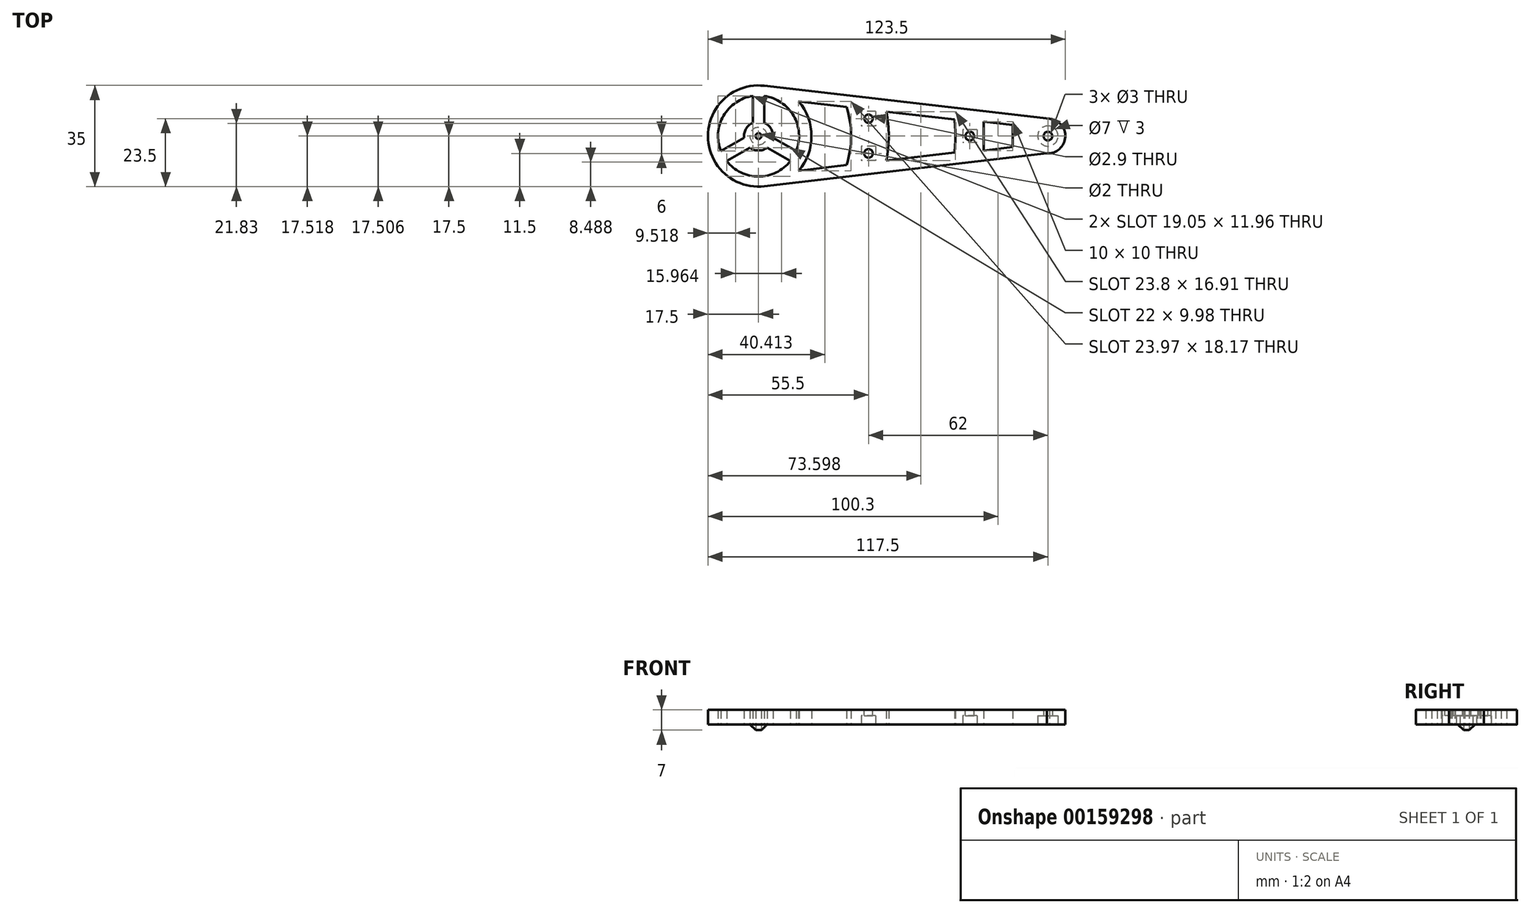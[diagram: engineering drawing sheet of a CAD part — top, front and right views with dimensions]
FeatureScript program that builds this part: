
annotation { "Feature Type Name" : "Feature", "Feature Type Description" : "" }
export const myFeature = defineFeature(function(context is Context, id is Id, definition is map)
    precondition{}
    {
        {
            var Q0;
            Q0=qCreatedBy(makeId("Top.planeOp"),FACE);
            var sketch = newSketch(context, id + "F0", { "sketchPlane" : qUnion([Q0])});
            skArc(sketch, "E0", {"start": v(2.01, 17.38) * mm, "mid": v(-17.5, 0) * mm, "end": v(2.03, -17.38) * mm});
            skArc(sketch, "E1", {"start": v(99.68, -6) * mm, "mid": v(105.99, -0.4) * mm, "end": v(100.47, 5.98) * mm});
            skLineSegment(sketch, "E2", {"start": v(100.47, 5.98) * mm, "end": v(2.01, 17.38) * mm});
            skLineSegment(sketch, "E3", {"start": v(99.68, -6) * mm, "end": v(2.03, -17.38) * mm});
            skArc(sketch, "E4", {"start": v(-2.97, -4.02) * mm, "mid": v(0, -5) * mm, "end": v(2.97, -4.02) * mm});
            skArc(sketch, "E5", {"start": v(-2, 13.86) * mm, "mid": v(-12.12, 7) * mm, "end": v(-13, -5.2) * mm});
            skArc(sketch, "E6", {"start": v(13.84, -11.98) * mm, "mid": v(18.3, 0) * mm, "end": v(13.83, 11.99) * mm});
            skArc(sketch, "E7", {"start": v(30.38, -10.05) * mm, "mid": v(32, 0.01) * mm, "end": v(30.37, 10.07) * mm});
            skLineSegment(sketch, "E8", {"start": v(13.83, 11.99) * mm, "end": v(30.37, 10.07) * mm});
            skLineSegment(sketch, "E9", {"start": v(13.84, -11.98) * mm, "end": v(30.38, -10.05) * mm});
            skLineSegment(sketch, "E10", {"start": v(-2, 13.86) * mm, "end": v(-2, 4.58) * mm});
            skLineSegment(sketch, "E11", {"start": v(2, 13.86) * mm, "end": v(2, 4.58) * mm});
            skLineSegment(sketch, "E12.1.0", {"start": v(-13, -5.2) * mm, "end": v(-4.97, -0.56) * mm});
            skLineSegment(sketch, "E12.1.1", {"start": v(-11, -8.66) * mm, "end": v(-2.97, -4.02) * mm});
            skLineSegment(sketch, "E12.2.0", {"start": v(11, -8.66) * mm, "end": v(2.97, -4.02) * mm});
            skLineSegment(sketch, "E12.2.1", {"start": v(13, -5.2) * mm, "end": v(4.97, -0.56) * mm});
            skArc(sketch, "E13.trimOffspring", {"start": v(13, -5.2) * mm, "mid": v(12.12, 7) * mm, "end": v(2, 13.86) * mm});
            skArc(sketch, "E14.trimOffspring", {"start": v(-11, -8.66) * mm, "mid": v(0, -14) * mm, "end": v(11, -8.66) * mm});
            skArc(sketch, "E15.trimOffspring", {"start": v(4.97, -0.56) * mm, "mid": v(4.33, 2.5) * mm, "end": v(2, 4.58) * mm});
            skArc(sketch, "E16.trimOffspring", {"start": v(-2, 4.58) * mm, "mid": v(-4.33, 2.5) * mm, "end": v(-4.97, -0.56) * mm});
            skCircle(sketch, "E17", {"center": v(0, 0) * mm, "radius": 1.5 * mm});
            skLineSegment(sketch, "E18", {"start": v(77.8, 5) * mm, "end": v(77.8, -5) * mm});
            skLineSegment(sketch, "E19", {"start": v(87.8, 3.84) * mm, "end": v(87.8, -3.83) * mm});
            skLineSegment(sketch, "E20", {"start": v(77.8, -5) * mm, "end": v(87.8, -3.83) * mm});
            skLineSegment(sketch, "E21", {"start": v(77.8, 5) * mm, "end": v(87.8, 3.84) * mm});
            skArc(sketch, "E22", {"start": v(44.2, -8.44) * mm, "mid": v(45, 0.02) * mm, "end": v(44.2, 8.47) * mm});
            skArc(sketch, "E23", {"start": v(67.76, -5.69) * mm, "mid": v(68, 0.03) * mm, "end": v(67.76, 5.74) * mm});
            skLineSegment(sketch, "E24", {"start": v(44.2, 8.47) * mm, "end": v(67.76, 5.74) * mm});
            skLineSegment(sketch, "E25", {"start": v(44.2, -8.44) * mm, "end": v(67.76, -5.69) * mm});
            skCircle(sketch, "E26", {"center": v(100, 0) * mm, "radius": 1.5 * mm});
            skSolve(sketch);
        }
        {
            var Q0;
            Q0 = qSketchRegion(id + "F0", true);
            extrude(context, id + "F1", {"entities" : qUnion([Q0]), "depth" : 5 * mm});
        }
        {
            var Q0;
            Q0=makeQuery(id+"F1.opExtrude","CAP_FACE",FACE,{"disambiguationData":[OSD([sQuery(id+"F0.wireOp",EDGE,"E0"),sQuery(id+"F0.wireOp",EDGE,"E1"),sQuery(id+"F0.wireOp",EDGE,"E2"),sQuery(id+"F0.wireOp",EDGE,"E3"),sQuery(id+"F0.wireOp",EDGE,"E4"),sQuery(id+"F0.wireOp",EDGE,"E5"),sQuery(id+"F0.wireOp",EDGE,"E6"),sQuery(id+"F0.wireOp",EDGE,"E7"),sQuery(id+"F0.wireOp",EDGE,"E8"),sQuery(id+"F0.wireOp",EDGE,"E9"),sQuery(id+"F0.wireOp",EDGE,"E10"),sQuery(id+"F0.wireOp",EDGE,"E11"),sQuery(id+"F0.wireOp",EDGE,"E12.1.0"),sQuery(id+"F0.wireOp",EDGE,"E12.1.1"),sQuery(id+"F0.wireOp",EDGE,"E12.2.0"),sQuery(id+"F0.wireOp",EDGE,"E12.2.1"),sQuery(id+"F0.wireOp",EDGE,"E13.trimOffspring"),sQuery(id+"F0.wireOp",EDGE,"E14.trimOffspring"),sQuery(id+"F0.wireOp",EDGE,"E15.trimOffspring"),sQuery(id+"F0.wireOp",EDGE,"E16.trimOffspring"),sQuery(id+"F0.wireOp",EDGE,"E17"),sQuery(id+"F0.wireOp",EDGE,"E18"),sQuery(id+"F0.wireOp",EDGE,"E19"),sQuery(id+"F0.wireOp",EDGE,"E20"),sQuery(id+"F0.wireOp",EDGE,"E21")])],"isStart":true});
            var sketch = newSketch(context, id + "F2", { "sketchPlane" : qUnion([Q0])});
            skLineSegment(sketch, "E27.bottom", {"start": v(40.5, 3.5) * mm, "end": v(35.5, 3.5) * mm});
            skLineSegment(sketch, "E27.top", {"start": v(40.5, 8.5) * mm, "end": v(35.5, 8.5) * mm});
            skLineSegment(sketch, "E27.left", {"start": v(40.5, 3.5) * mm, "end": v(40.5, 8.5) * mm});
            skLineSegment(sketch, "E27.right", {"start": v(35.5, 3.5) * mm, "end": v(35.5, 8.5) * mm});
            skPoint(sketch, "E27.middle", {"position": v(38, 6) * mm});
            skLineSegment(sketch, "E28.bottom", {"start": v(75.5, -2.25) * mm, "end": v(70.5, -2.25) * mm});
            skLineSegment(sketch, "E28.top", {"start": v(75.5, 2.25) * mm, "end": v(70.5, 2.25) * mm});
            skLineSegment(sketch, "E28.left", {"start": v(75.5, -2.25) * mm, "end": v(75.5, 2.25) * mm});
            skLineSegment(sketch, "E28.right", {"start": v(70.5, -2.25) * mm, "end": v(70.5, 2.25) * mm});
            skPoint(sketch, "E28.middle", {"position": v(73, 0) * mm});
            skLineSegment(sketch, "E29.bottom", {"start": v(40.5, -8.5) * mm, "end": v(35.5, -8.5) * mm});
            skLineSegment(sketch, "E29.top", {"start": v(40.5, -3.5) * mm, "end": v(35.5, -3.5) * mm});
            skLineSegment(sketch, "E29.left", {"start": v(40.5, -8.5) * mm, "end": v(40.5, -3.5) * mm});
            skLineSegment(sketch, "E29.right", {"start": v(35.5, -8.5) * mm, "end": v(35.5, -3.5) * mm});
            skPoint(sketch, "E29.middle", {"position": v(38, -6) * mm});
            skCircle(sketch, "E30", {"center": v(100, 0) * mm, "radius": 3.5 * mm});
            skSolve(sketch);
        }
        {
            var Q0;
            Q0 = qSketchRegion(id + "F2", true);
            extrude(context, id + "F3", {"entities" : qUnion([Q0]), "operationType" : NewBodyOperationType.REMOVE, "oppositeDirection" : true, "depth" : 3 * mm});
        }
        {
            var Q0;
            Q0=makeQuery(id+"F1.opExtrude","CAP_FACE",FACE,{"disambiguationData":[OSD([sQuery(id+"F0.wireOp",EDGE,"E0"),sQuery(id+"F0.wireOp",EDGE,"E1"),sQuery(id+"F0.wireOp",EDGE,"E2"),sQuery(id+"F0.wireOp",EDGE,"E3"),sQuery(id+"F0.wireOp",EDGE,"E4"),sQuery(id+"F0.wireOp",EDGE,"E5"),sQuery(id+"F0.wireOp",EDGE,"E6"),sQuery(id+"F0.wireOp",EDGE,"E7"),sQuery(id+"F0.wireOp",EDGE,"E8"),sQuery(id+"F0.wireOp",EDGE,"E9"),sQuery(id+"F0.wireOp",EDGE,"E10"),sQuery(id+"F0.wireOp",EDGE,"E11"),sQuery(id+"F0.wireOp",EDGE,"E12.1.0"),sQuery(id+"F0.wireOp",EDGE,"E12.1.1"),sQuery(id+"F0.wireOp",EDGE,"E12.2.0"),sQuery(id+"F0.wireOp",EDGE,"E12.2.1"),sQuery(id+"F0.wireOp",EDGE,"E13.trimOffspring"),sQuery(id+"F0.wireOp",EDGE,"E14.trimOffspring"),sQuery(id+"F0.wireOp",EDGE,"E15.trimOffspring"),sQuery(id+"F0.wireOp",EDGE,"E16.trimOffspring"),sQuery(id+"F0.wireOp",EDGE,"E17"),sQuery(id+"F0.wireOp",EDGE,"E18"),sQuery(id+"F0.wireOp",EDGE,"E19"),sQuery(id+"F0.wireOp",EDGE,"E20"),sQuery(id+"F0.wireOp",EDGE,"E21")])],"isStart":false});
            var sketch = newSketch(context, id + "F4", { "sketchPlane" : qUnion([Q0])});
            skCircle(sketch, "E31", {"center": v(38, -6) * mm, "radius": 1.5 * mm});
            skCircle(sketch, "E32", {"center": v(73, 0) * mm, "radius": 1.5 * mm});
            skCircle(sketch, "E33", {"center": v(38, 6) * mm, "radius": 1.45 * mm});
            skSolve(sketch);
        }
        {
            var Q0;
            Q0 = qSketchRegion(id + "F4", true);
            extrude(context, id + "F5", {"entities" : qUnion([Q0]), "operationType" : NewBodyOperationType.REMOVE, "oppositeDirection" : true, "depth" : 25 * mm});
        }
        {
            var Q0;
            Q0=makeQuery(id+"F1.opExtrude","CAP_FACE",FACE,{"disambiguationData":[OSD([sQuery(id+"F0.wireOp",EDGE,"E0"),sQuery(id+"F0.wireOp",EDGE,"E1"),sQuery(id+"F0.wireOp",EDGE,"E2"),sQuery(id+"F0.wireOp",EDGE,"E3"),sQuery(id+"F0.wireOp",EDGE,"E4"),sQuery(id+"F0.wireOp",EDGE,"E5"),sQuery(id+"F0.wireOp",EDGE,"E6"),sQuery(id+"F0.wireOp",EDGE,"E7"),sQuery(id+"F0.wireOp",EDGE,"E8"),sQuery(id+"F0.wireOp",EDGE,"E9"),sQuery(id+"F0.wireOp",EDGE,"E10"),sQuery(id+"F0.wireOp",EDGE,"E11"),sQuery(id+"F0.wireOp",EDGE,"E12.1.0"),sQuery(id+"F0.wireOp",EDGE,"E12.1.1"),sQuery(id+"F0.wireOp",EDGE,"E12.2.0"),sQuery(id+"F0.wireOp",EDGE,"E12.2.1"),sQuery(id+"F0.wireOp",EDGE,"E13.trimOffspring"),sQuery(id+"F0.wireOp",EDGE,"E14.trimOffspring"),sQuery(id+"F0.wireOp",EDGE,"E15.trimOffspring"),sQuery(id+"F0.wireOp",EDGE,"E16.trimOffspring"),sQuery(id+"F0.wireOp",EDGE,"E17"),sQuery(id+"F0.wireOp",EDGE,"E18"),sQuery(id+"F0.wireOp",EDGE,"E19"),sQuery(id+"F0.wireOp",EDGE,"E20"),sQuery(id+"F0.wireOp",EDGE,"E21")])],"isStart":false});
            var sketch = newSketch(context, id + "F6", { "sketchPlane" : qUnion([Q0])});
            skCircle(sketch, "E34", {"center": v(0, 0) * mm, "radius": 3 * mm});
            skSolve(sketch);
        }
        {
            var Q0;
            Q0 = qSketchRegion(id + "F6", true);
            extrude(context, id + "F7", {"entities" : qUnion([Q0]), "operationType" : NewBodyOperationType.ADD, "oppositeDirection" : true, "depth" : 7 * mm});
        }
        {
            var Q0;
            Q0=makeQuery(id+"F7.opExtrude","CAP_EDGE",EDGE,{"disambiguationData":[OSD([sQuery(id+"F6.wireOp",EDGE,"E34")])],"isStart":false});
            chamfer(context, id + "F8", {"entities" : qUnion([Q0]), "width" : 2 * mm, "tangentPropagation" : true});
        }
        {
            var Q0;
            Q0=makeQuery(id+"F7.opExtrude","CAP_FACE",FACE,{"disambiguationData":[OSD([sQuery(id+"F6.wireOp",EDGE,"E34")])],"isStart":false});
            extrude(context, id + "F9", {"entities" : qUnion([Q0]), "operationType" : NewBodyOperationType.REMOVE, "oppositeDirection" : true, "depth" : 25 * mm});
        }
    });
